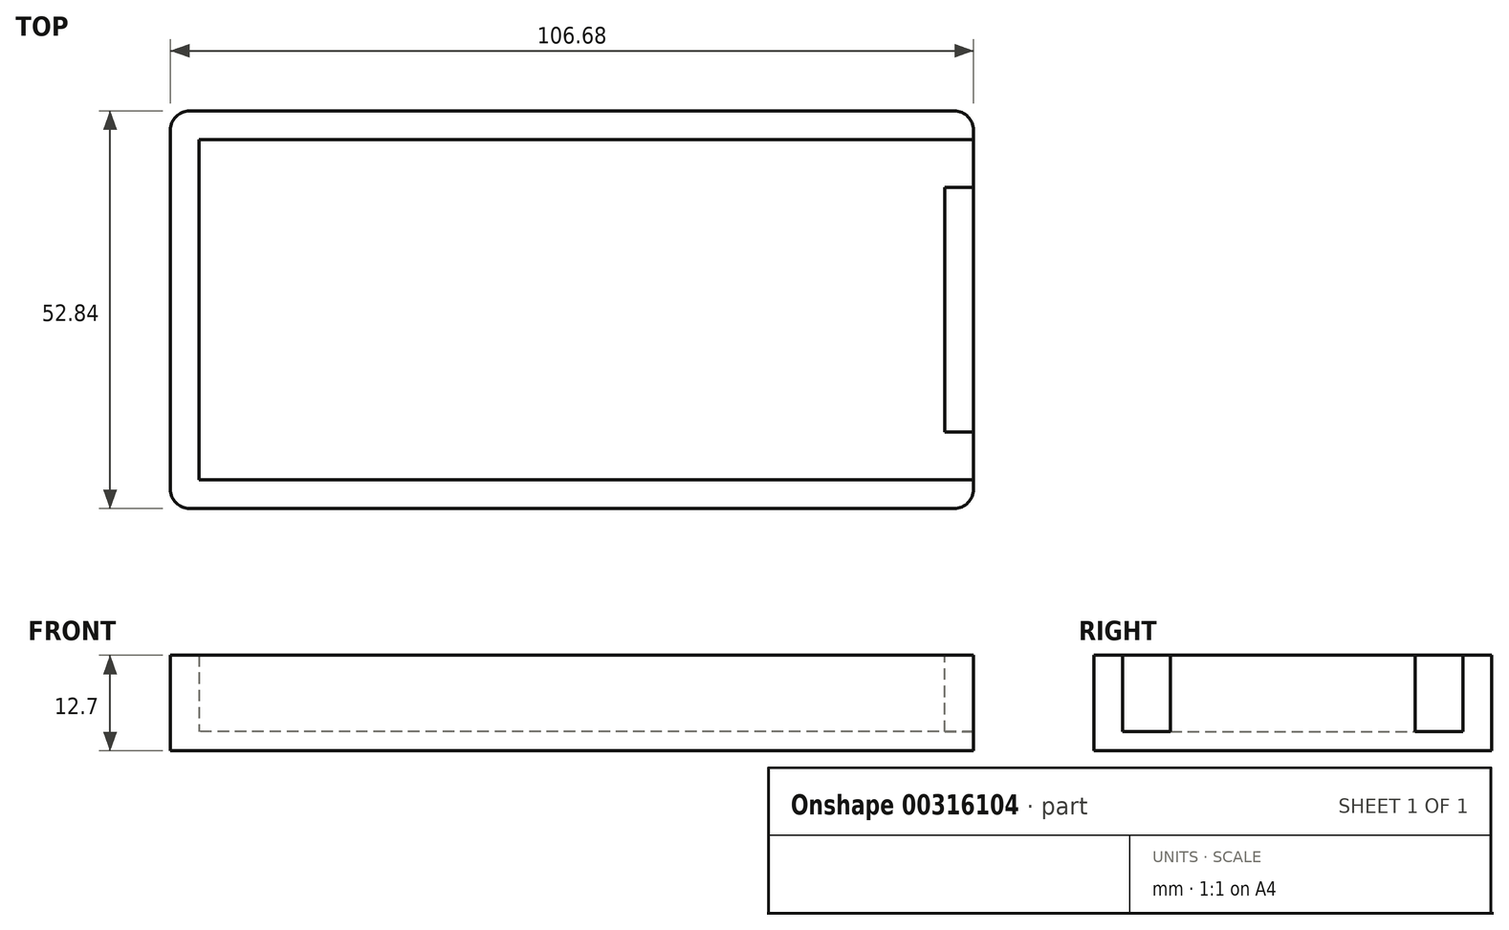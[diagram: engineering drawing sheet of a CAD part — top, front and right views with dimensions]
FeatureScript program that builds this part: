
annotation { "Feature Type Name" : "Feature", "Feature Type Description" : "" }
export const myFeature = defineFeature(function(context is Context, id is Id, definition is map)
    precondition{}
    {
        {
            var Q0;
            Q0=qCreatedBy(makeId("Top.planeOp"),FACE);
            var sketch = newSketch(context, id + "F0", { "sketchPlane" : qUnion([Q0])});
            skLineSegment(sketch, "E0.bottom", {"start": v(49.53, 22.6) * mm, "end": v(-49.53, 22.6) * mm});
            skLineSegment(sketch, "E0.top", {"start": v(49.53, -22.6) * mm, "end": v(-49.53, -22.6) * mm});
            skLineSegment(sketch, "E0.left", {"start": v(49.53, 22.6) * mm, "end": v(49.53, -22.6) * mm});
            skLineSegment(sketch, "E0.right", {"start": v(-49.53, 22.6) * mm, "end": v(-49.53, -22.6) * mm});
            skPoint(sketch, "E0.middle", {"position": v(0, 0) * mm});
            skLineSegment(sketch, "E1.bottom", {"start": v(53.34, 26.42) * mm, "end": v(-53.34, 26.42) * mm});
            skLineSegment(sketch, "E1.top", {"start": v(53.34, -26.42) * mm, "end": v(-53.34, -26.42) * mm});
            skLineSegment(sketch, "E1.left", {"start": v(53.34, 26.42) * mm, "end": v(53.34, -26.42) * mm});
            skLineSegment(sketch, "E1.right", {"start": v(-53.34, 26.42) * mm, "end": v(-53.34, -26.42) * mm});
            skSolve(sketch);
        }
        {
            var Q0;
            Q0=makeQuery(id+"F0.imprint","IMPRINT",FACE,{"disambiguationData":[TD([[makeQuery(id+"F0.imprint","IMPRINT",EDGE,{"derivedFrom":sQuery(id+"F0.wireOp",EDGE,"E0.bottom")}),-1.0]])]});
            extrude(context, id + "F1", {"entities" : qUnion([Q0]), "depth" : 12.7 * mm});
        }
        {
            var Q0;
            Q0=qCreatedBy(makeId("Top.planeOp"),FACE);
            var sketch = newSketch(context, id + "F2", { "sketchPlane" : qUnion([Q0])});
            skLineSegment(sketch, "E2.bottom", {"start": v(49.53, -22.6) * mm, "end": v(-49.53, -22.6) * mm});
            skLineSegment(sketch, "E2.top", {"start": v(49.53, 22.6) * mm, "end": v(-49.53, 22.6) * mm});
            skLineSegment(sketch, "E2.left", {"start": v(49.53, -22.6) * mm, "end": v(49.53, 22.6) * mm});
            skLineSegment(sketch, "E2.right", {"start": v(-49.53, -22.6) * mm, "end": v(-49.53, 22.6) * mm});
            skPoint(sketch, "E2.middle", {"position": v(0, 0) * mm});
            skSolve(sketch);
        }
        {
            var Q0;
            Q0 = qSketchRegion(id + "F2", true);
            extrude(context, id + "F3", {"entities" : qUnion([Q0]), "operationType" : NewBodyOperationType.ADD, "depth" : 2.54 * mm});
        }
        {
            var Q0;
            Q0=makeQuery(id+"F1.opExtrude","CAP_FACE",FACE,{"disambiguationData":[OSD([sQuery(id+"F0.wireOp",EDGE,"E0.bottom"),sQuery(id+"F0.wireOp",EDGE,"E0.top"),sQuery(id+"F0.wireOp",EDGE,"E0.left"),sQuery(id+"F0.wireOp",EDGE,"E0.right"),sQuery(id+"F0.wireOp",EDGE,"E1.bottom"),sQuery(id+"F0.wireOp",EDGE,"E1.top"),sQuery(id+"F0.wireOp",EDGE,"E1.left"),sQuery(id+"F0.wireOp",EDGE,"E1.right")])],"isStart":false});
            var sketch = newSketch(context, id + "F4", { "sketchPlane" : qUnion([Q0])});
            skLineSegment(sketch, "E3.bottom", {"start": v(49.53, 22.6) * mm, "end": v(53.34, 22.6) * mm});
            skLineSegment(sketch, "E3.top", {"start": v(49.53, 16.26) * mm, "end": v(53.34, 16.26) * mm});
            skLineSegment(sketch, "E3.left", {"start": v(49.53, 22.6) * mm, "end": v(49.53, 16.26) * mm});
            skLineSegment(sketch, "E3.right", {"start": v(53.34, 22.6) * mm, "end": v(53.34, 16.26) * mm});
            skLineSegment(sketch, "E4.bottom", {"start": v(49.53, -22.6) * mm, "end": v(53.34, -22.6) * mm});
            skLineSegment(sketch, "E4.top", {"start": v(49.53, -16.26) * mm, "end": v(53.34, -16.26) * mm});
            skLineSegment(sketch, "E4.left", {"start": v(49.53, -22.6) * mm, "end": v(49.53, -16.26) * mm});
            skLineSegment(sketch, "E4.right", {"start": v(53.34, -22.6) * mm, "end": v(53.34, -16.26) * mm});
            skSolve(sketch);
        }
        {
            var Q0;
            Q0 = qSketchRegion(id + "F4", true);
            extrude(context, id + "F5", {"entities" : qUnion([Q0]), "operationType" : NewBodyOperationType.REMOVE, "oppositeDirection" : true, "depth" : 10.16 * mm});
        }
        {
            var Q0;
            Q0=makeQuery(id+"F5.boolean.opBoolean","COPY",EDGE,{"derivedFrom":makeQuery(id+"F5.opExtrude","SWEPT_EDGE",EDGE,{"disambiguationData":[OSD([sQuery(id+"F0.wireOp",EDGE,"E0.left"),sQuery(id+"F4.wireOp",EDGE,"E3.top"),sQuery(id+"F4.wireOp",EDGE,"E3.left")])]})});
            var Q1;
            Q1=makeQuery(id+"F5.boolean.opBoolean","COPY",EDGE,{"derivedFrom":makeQuery(id+"F5.opExtrude","SWEPT_EDGE",EDGE,{"disambiguationData":[OSD([sQuery(id+"F0.wireOp",EDGE,"E1.left"),sQuery(id+"F4.wireOp",EDGE,"E3.bottom"),sQuery(id+"F4.wireOp",EDGE,"E3.right")])]})});
            var Q2;
            Q2=makeQuery(id+"F5.boolean.opBoolean","COPY",EDGE,{"derivedFrom":makeQuery(id+"F5.opExtrude","SWEPT_EDGE",EDGE,{"disambiguationData":[OSD([sQuery(id+"F0.wireOp",EDGE,"E0.left"),sQuery(id+"F4.wireOp",EDGE,"E4.top"),sQuery(id+"F4.wireOp",EDGE,"E4.left")])]})});
            var Q3;
            Q3=makeQuery(id+"F5.boolean.opBoolean","COPY",EDGE,{"derivedFrom":makeQuery(id+"F5.opExtrude","SWEPT_EDGE",EDGE,{"disambiguationData":[OSD([sQuery(id+"F0.wireOp",EDGE,"E1.left"),sQuery(id+"F4.wireOp",EDGE,"E4.bottom"),sQuery(id+"F4.wireOp",EDGE,"E4.right")])]})});
            var Q4;
            Q4=makeQuery(id+"F1.opExtrude","SWEPT_EDGE",EDGE,{"disambiguationData":[OSD([sQuery(id+"F0.wireOp",EDGE,"E1.bottom"),sQuery(id+"F0.wireOp",EDGE,"E1.left")])]});
            var Q5;
            Q5=makeQuery(id+"F1.opExtrude","SWEPT_EDGE",EDGE,{"disambiguationData":[OSD([sQuery(id+"F0.wireOp",EDGE,"E1.top"),sQuery(id+"F0.wireOp",EDGE,"E1.left")])]});
            var Q6;
            Q6=makeQuery(id+"F1.opExtrude","SWEPT_EDGE",EDGE,{"disambiguationData":[OSD([sQuery(id+"F0.wireOp",EDGE,"E1.top"),sQuery(id+"F0.wireOp",EDGE,"E1.right")])]});
            var Q7;
            Q7=makeQuery(id+"F1.opExtrude","SWEPT_EDGE",EDGE,{"disambiguationData":[OSD([sQuery(id+"F0.wireOp",EDGE,"E1.bottom"),sQuery(id+"F0.wireOp",EDGE,"E1.right")])]});
            fillet(context, id + "F6", {"entities" : qUnion([Q0, Q1, Q2, Q3, Q4, Q5, Q6, Q7]), "radius" : 2.54 * mm, "tangentPropagation" : true, "allowEdgeOverflow" : false});
        }
    });
